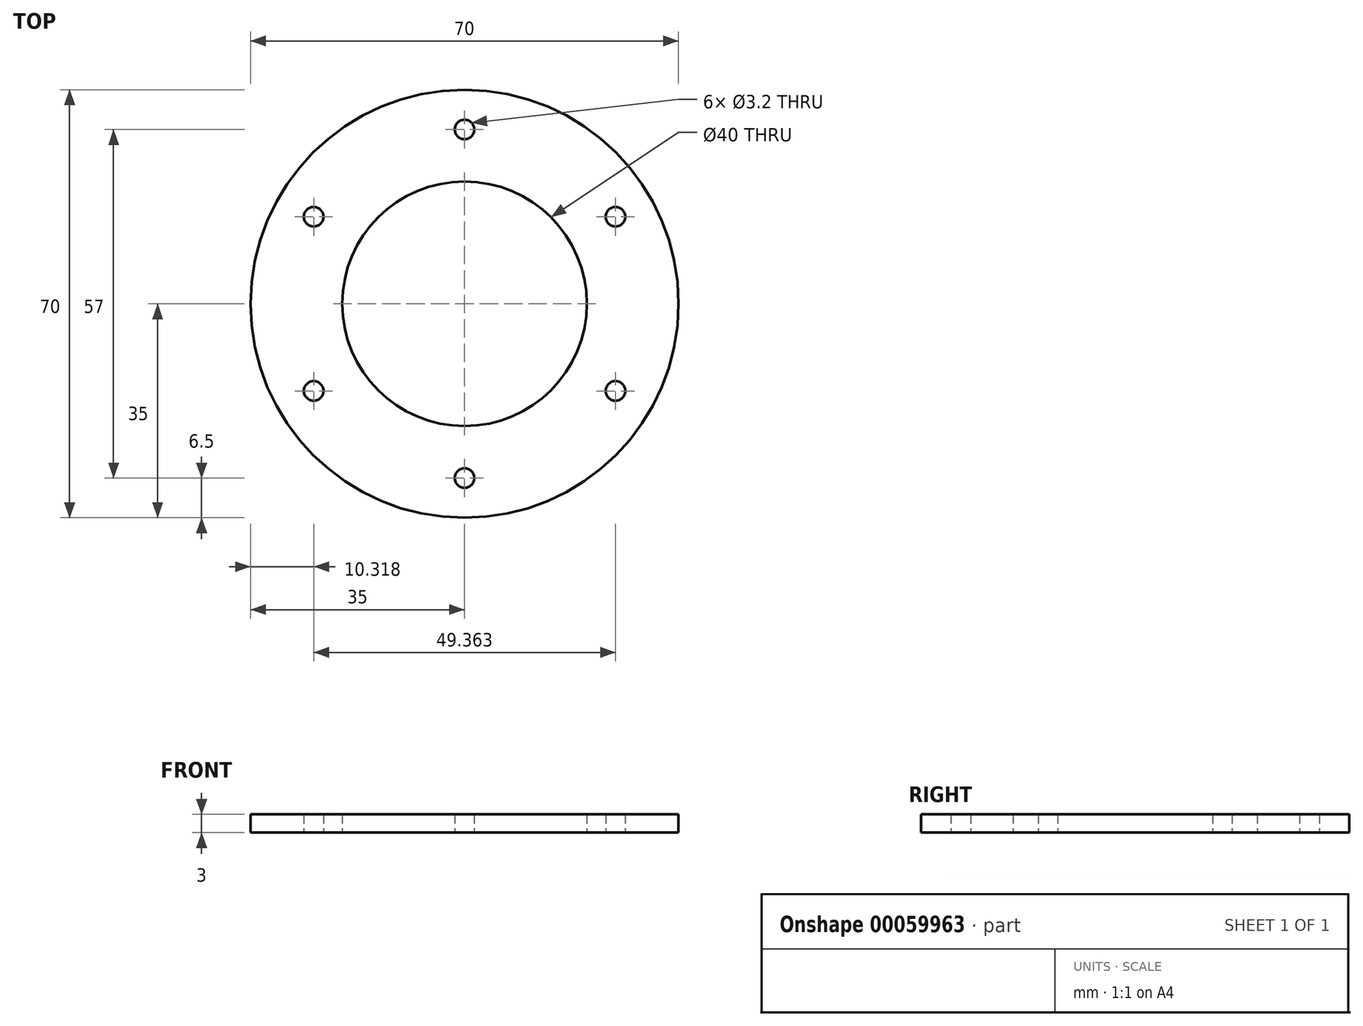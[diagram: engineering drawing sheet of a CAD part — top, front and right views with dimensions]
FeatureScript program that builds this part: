
annotation { "Feature Type Name" : "Feature", "Feature Type Description" : "" }
export const myFeature = defineFeature(function(context is Context, id is Id, definition is map)
    precondition{}
    {
        {
            var Q0;
            Q0=qCreatedBy(makeId("Top.planeOp"),FACE);
            var sketch = newSketch(context, id + "F0", { "sketchPlane" : qUnion([Q0])});
            skCircle(sketch, "E0", {"center": v(0, 0) * mm, "radius": 35 * mm});
            skCircle(sketch, "E1", {"center": v(0, 0) * mm, "radius": 22.5 * mm});
            skCircle(sketch, "E2", {"center": v(0, 0) * mm, "radius": 20 * mm});
            skCircle(sketch, "E3", {"center": v(0, 28.5) * mm, "radius": 1.6 * mm});
            skCircle(sketch, "E4.1.0", {"center": v(-24.68, 14.25) * mm, "radius": 1.6 * mm});
            skCircle(sketch, "E4.2.0", {"center": v(-24.68, -14.25) * mm, "radius": 1.6 * mm});
            skCircle(sketch, "E4.3.0", {"center": v(0, -28.5) * mm, "radius": 1.6 * mm});
            skCircle(sketch, "E4.4.0", {"center": v(24.68, -14.25) * mm, "radius": 1.6 * mm});
            skCircle(sketch, "E4.5.0", {"center": v(24.68, 14.25) * mm, "radius": 1.6 * mm});
            skSolve(sketch);
        }
        {
            var Q0;
            Q0=makeQuery(id+"F0.imprint","IMPRINT",FACE,{"disambiguationData":[TD([[makeQuery(id+"F0.imprint","IMPRINT",EDGE,{"derivedFrom":sQuery(id+"F0.wireOp",EDGE,"E1")}),1.0]])]});
            extrude(context, id + "F1", {"entities" : qUnion([Q0]), "depth" : 3 * mm});
        }
        {
            var Q0;
            Q0=makeQuery(id+"F0.imprint","IMPRINT",FACE,{"disambiguationData":[TD([[makeQuery(id+"F0.imprint","IMPRINT",EDGE,{"derivedFrom":sQuery(id+"F0.wireOp",EDGE,"E0")}),1.0]])]});
            extrude(context, id + "F2", {"entities" : qUnion([Q0]), "operationType" : NewBodyOperationType.ADD, "depth" : 3 * mm});
        }
    });
